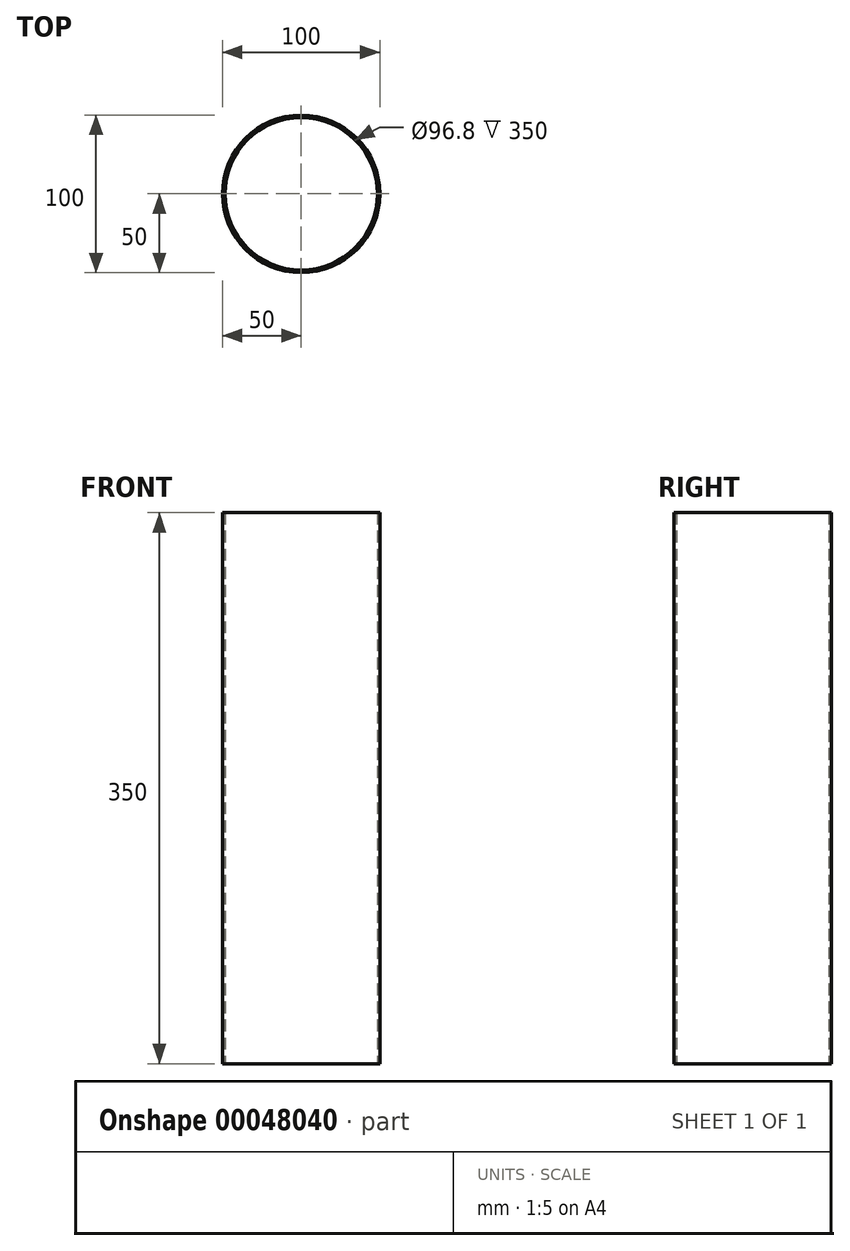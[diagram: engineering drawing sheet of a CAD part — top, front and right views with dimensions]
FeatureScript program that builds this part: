
annotation { "Feature Type Name" : "Feature", "Feature Type Description" : "" }
export const myFeature = defineFeature(function(context is Context, id is Id, definition is map)
    precondition{}
    {
        {
            var Q0;
            Q0=qCreatedBy(makeId("Top.planeOp"),FACE);
            var sketch = newSketch(context, id + "F0", { "sketchPlane" : qUnion([Q0])});
            skCircle(sketch, "E0", {"center": v(0, 0) * mm, "radius": 48.4 * mm});
            skCircle(sketch, "E1.0", {"center": v(0, 0) * mm, "radius": 50 * mm});
            skSolve(sketch);
        }
        {
            var Q0;
            Q0 = qSketchRegion(id + "F0", true);
            extrude(context, id + "F1", {"entities" : qUnion([Q0]), "depth" : 350 * mm});
        }
    });
